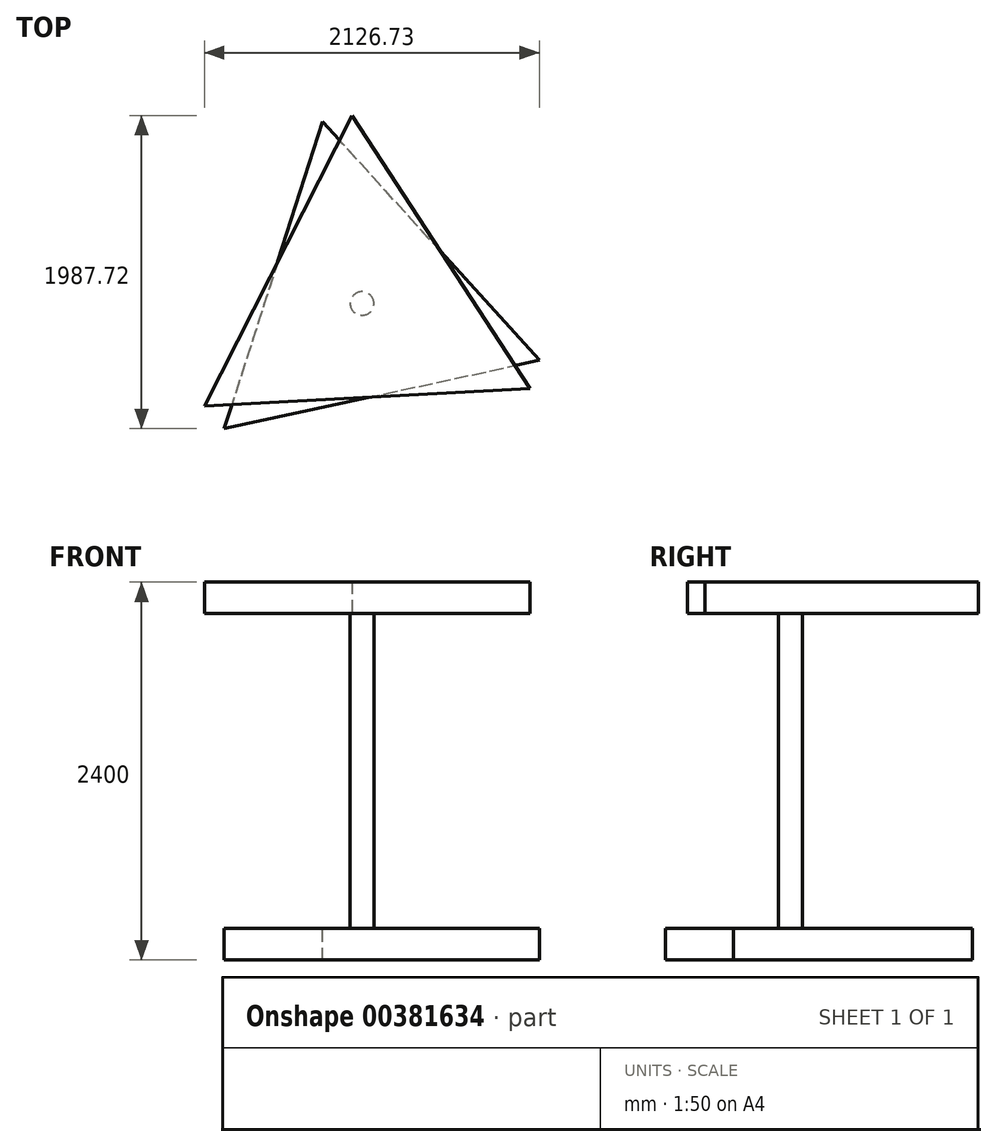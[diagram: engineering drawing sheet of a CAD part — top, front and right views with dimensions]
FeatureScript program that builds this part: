
annotation { "Feature Type Name" : "Feature", "Feature Type Description" : "" }
export const myFeature = defineFeature(function(context is Context, id is Id, definition is map)
    precondition{}
    {
        {
            var Q0;
            Q0=qCreatedBy(makeId("Top.planeOp"),FACE);
            var sketch = newSketch(context, id + "F0", { "sketchPlane" : qUnion([Q0])});
            skCircle(sketch, "E0", {"center": v(0, 0) * mm, "radius": 75.34 * mm});
            skSolve(sketch);
        }
        {
            var Q0;
            Q0 = qSketchRegion(id + "F0", true);
            extrude(context, id + "F1", {"entities" : qUnion([Q0]), "depth" : 2000 * mm});
        }
        {
            var Q0;
            Q0=makeQuery(id+"F1.opExtrude","CAP_FACE",FACE,{"disambiguationData":[OSD([sQuery(id+"F0.wireOp",EDGE,"E0")])],"isStart":false});
            var sketch = newSketch(context, id + "F2", { "sketchPlane" : qUnion([Q0])});
            skCircle(sketch, "E1.cCircle", {"center": v(0, 0) * mm, "radius": 597.53 * mm, "construction": true});
            skLineSegment(sketch, "E1.0", {"start": v(-64.5, 1193.32) * mm, "end": v(1065.7, -540.8) * mm});
            skLineSegment(sketch, "E1.1", {"start": v(1065.7, -540.8) * mm, "end": v(-1001.2, -652.52) * mm});
            skLineSegment(sketch, "E1.2", {"start": v(-1001.2, -652.52) * mm, "end": v(-64.5, 1193.32) * mm});
            skPoint(sketch, "E1.0.midPoint", {"position": v(500.6, 326.26) * mm});
            skSolve(sketch);
        }
        {
            var Q0;
            Q0 = qSketchRegion(id + "F2", true);
            extrude(context, id + "F3", {"entities" : qUnion([Q0]), "operationType" : NewBodyOperationType.ADD, "depth" : 200 * mm});
        }
        {
            var Q0;
            Q0=makeQuery(id+"F1.opExtrude","CAP_FACE",FACE,{"disambiguationData":[OSD([sQuery(id+"F0.wireOp",EDGE,"E0")])],"isStart":true});
            var sketch = newSketch(context, id + "F4", { "sketchPlane" : qUnion([Q0])});
            skCircle(sketch, "E2.cCircle", {"center": v(0, 0) * mm, "radius": 590.95 * mm, "construction": true});
            skLineSegment(sketch, "E2.0", {"start": v(-875.1, 794.4) * mm, "end": v(1125.53, 360.66) * mm});
            skLineSegment(sketch, "E2.1", {"start": v(1125.53, 360.66) * mm, "end": v(-250.42, -1155.06) * mm});
            skLineSegment(sketch, "E2.2", {"start": v(-250.42, -1155.06) * mm, "end": v(-875.1, 794.4) * mm});
            skPoint(sketch, "E2.0.midPoint", {"position": v(125.21, 577.53) * mm});
            skSolve(sketch);
        }
        {
            var Q0;
            Q0 = qSketchRegion(id + "F4", true);
            extrude(context, id + "F5", {"entities" : qUnion([Q0]), "operationType" : NewBodyOperationType.ADD, "depth" : 200 * mm});
        }
    });
